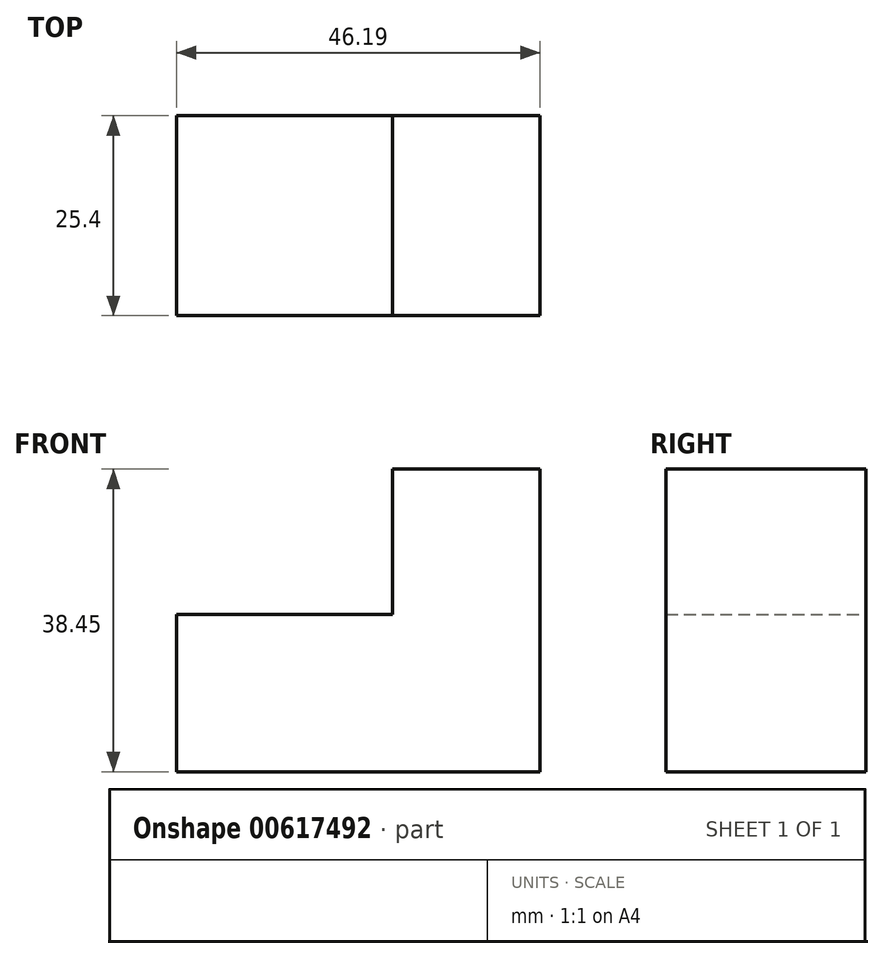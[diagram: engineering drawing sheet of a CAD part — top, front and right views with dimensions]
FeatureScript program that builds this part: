
annotation { "Feature Type Name" : "Feature", "Feature Type Description" : "" }
export const myFeature = defineFeature(function(context is Context, id is Id, definition is map)
    precondition{}
    {
        {
            var Q0;
            Q0=qCreatedBy(makeId("Front.planeOp"),FACE);
            var sketch = newSketch(context, id + "F0", { "sketchPlane" : qUnion([Q0])});
            skLineSegment(sketch, "E0", {"start": v(0, 0) * mm, "end": v(0, 38.45) * mm});
            skLineSegment(sketch, "E1", {"start": v(0, 38.45) * mm, "end": v(-18.74, 38.45) * mm});
            skLineSegment(sketch, "E2", {"start": v(-18.74, 38.45) * mm, "end": v(-18.74, 20) * mm});
            skLineSegment(sketch, "E3", {"start": v(-18.74, 20) * mm, "end": v(-46.2, 20) * mm});
            skLineSegment(sketch, "E4", {"start": v(-46.2, 20) * mm, "end": v(-46.2, 0) * mm});
            skLineSegment(sketch, "E5", {"start": v(-46.2, 0) * mm, "end": v(0, 0) * mm});
            skLineSegment(sketch, "E6", {"start": v(26.72, 44.62) * mm, "end": v(26.72, 0) * mm});
            skLineSegment(sketch, "E7", {"start": v(26.72, 0) * mm, "end": v(46.6, 0) * mm});
            skLineSegment(sketch, "E8", {"start": v(46.6, 0) * mm, "end": v(46.6, 44.62) * mm});
            skLineSegment(sketch, "E9", {"start": v(46.6, 44.62) * mm, "end": v(26.72, 44.62) * mm});
            skSolve(sketch);
        }
        {
            var Q0;
            Q0=makeQuery(id+"F0.imprint","IMPRINT",FACE,{"disambiguationData":[TD([[makeQuery(id+"F0.imprint","IMPRINT",EDGE,{"derivedFrom":sQuery(id+"F0.wireOp",EDGE,"E0")}),1.0]])]});
            extrude(context, id + "F1", {"entities" : qUnion([Q0]), "depth" : 25.4 * mm, "offsetDistance" : 25.4 * mm});
        }
    });
